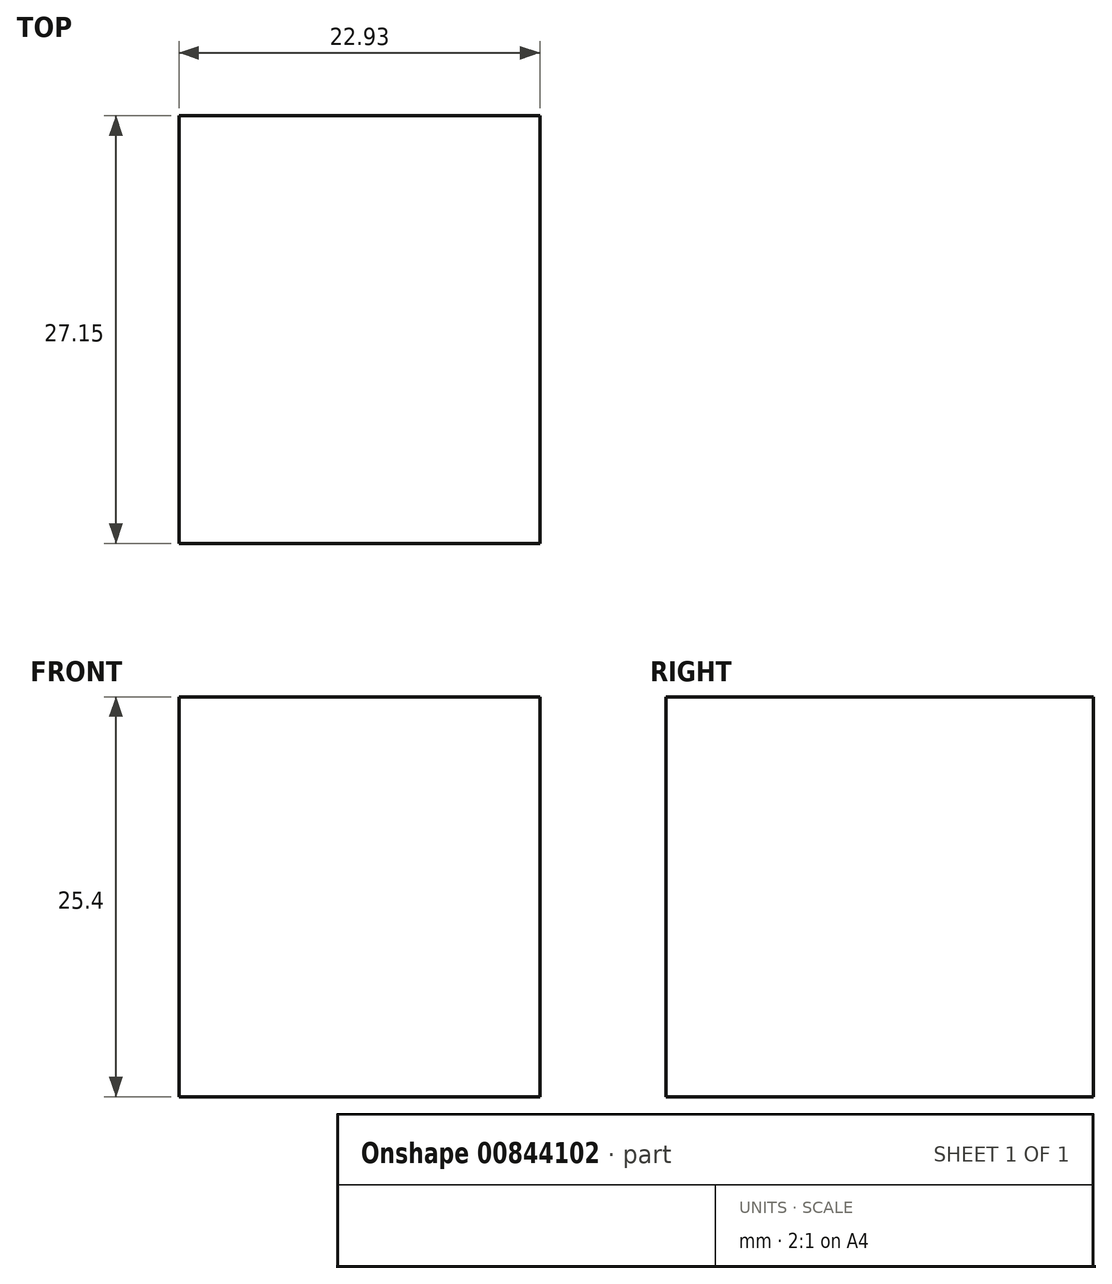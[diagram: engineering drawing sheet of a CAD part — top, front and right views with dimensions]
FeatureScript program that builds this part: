
annotation { "Feature Type Name" : "Feature", "Feature Type Description" : "" }
export const myFeature = defineFeature(function(context is Context, id is Id, definition is map)
    precondition{}
    {
        {
            var Q0;
            Q0=qCreatedBy(makeId("Top.planeOp"),FACE);
            var sketch = newSketch(context, id + "F0", { "sketchPlane" : qUnion([Q0])});
            skLineSegment(sketch, "E0.bottom", {"start": v(-10.78, -14.06) * mm, "end": v(12.15, -14.06) * mm});
            skLineSegment(sketch, "E0.top", {"start": v(-10.78, 13.1) * mm, "end": v(12.15, 13.1) * mm});
            skLineSegment(sketch, "E0.left", {"start": v(-10.78, -14.06) * mm, "end": v(-10.78, 13.1) * mm});
            skLineSegment(sketch, "E0.right", {"start": v(12.15, -14.06) * mm, "end": v(12.15, 13.1) * mm});
            skSolve(sketch);
        }
        {
            var Q0;
            Q0 = qSketchRegion(id + "F0", true);
            extrude(context, id + "F1", {"entities" : qUnion([Q0]), "depth" : 25.4 * mm, "offsetDistance" : 25.4 * mm});
        }
    });
